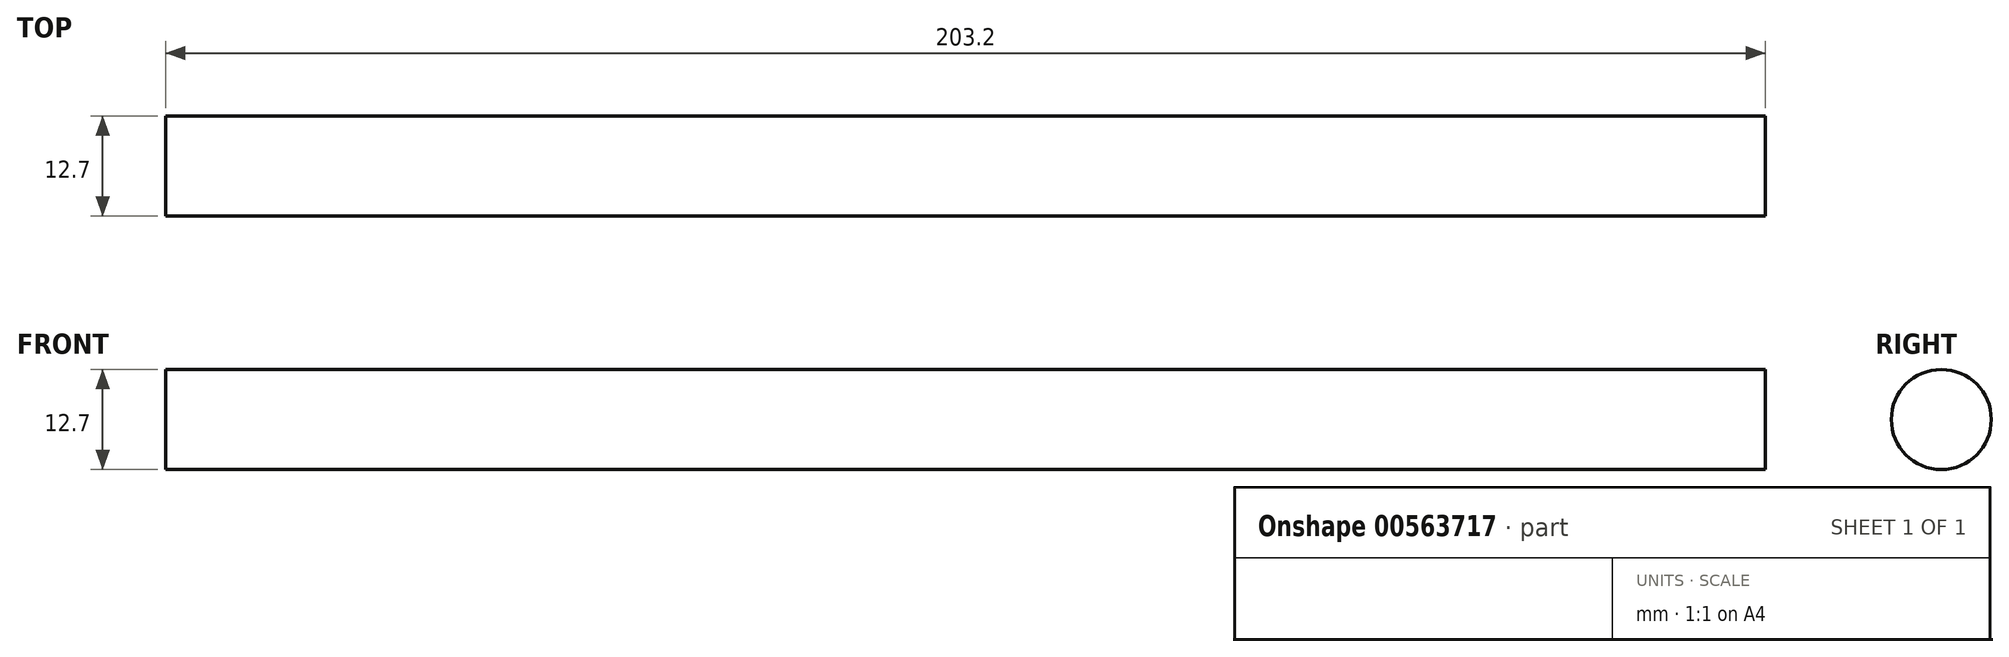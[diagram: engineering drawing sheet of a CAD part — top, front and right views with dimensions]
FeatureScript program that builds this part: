
annotation { "Feature Type Name" : "Feature", "Feature Type Description" : "" }
export const myFeature = defineFeature(function(context is Context, id is Id, definition is map)
    precondition{}
    {
        {
            var Q0;
            Q0=qCreatedBy(makeId("Right.planeOp"),FACE);
            var sketch = newSketch(context, id + "F0", { "sketchPlane" : qUnion([Q0])});
            skCircle(sketch, "E0", {"center": v(0, 1.54) * mm, "radius": 6.35 * mm});
            skSolve(sketch);
        }
        {
            var Q0;
            Q0=makeQuery(id+"F0.imprint","IMPRINT",FACE,{"disambiguationData":[TD([[makeQuery(id+"F0.imprint","IMPRINT",EDGE,{"derivedFrom":sQuery(id+"F0.wireOp",EDGE,"E0")}),1.0]])]});
            extrude(context, id + "F1", {"entities" : qUnion([Q0]), "depth" : 203.2 * mm});
        }
    });
